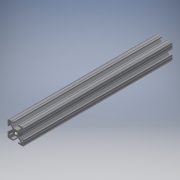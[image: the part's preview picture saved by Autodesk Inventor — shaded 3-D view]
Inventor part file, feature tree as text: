
AUTODESK INVENTOR PART (.ipt)
format: ipt  version: 2018 (Build 220112000, 112)  size: 227,840 bytes
history: native  units: in
note: dims shown in document units (in); Inventor stores cm internally (conversion verified against a paired STEP export)
features: sketch x2, extrude x1
ambient origin geometry x8: Origin, YZ Plane, XZ Plane, XY Plane, X Axis, Y Axis, Z Axis, Center Point
bodies: Solid1 (feature_tree)
feature tree (3):
  extrude  "Extrusion1"  [1 undecoded]
  sketch  "Sketch2"
  sketch  "Sketch1"  dims[d0=9.0in d1=0.0in]
note: 1 required parameter value undecoded (feature->parameter linkage not recoverable at this tier; creation-order binding heuristic only, values carry confidence <= 0.55)
